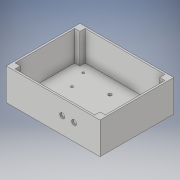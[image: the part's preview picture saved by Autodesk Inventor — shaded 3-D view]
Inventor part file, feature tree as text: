
AUTODESK INVENTOR PART (.ipt)
format: ipt  version: 2018 (Build 220112000, 112)  size: 164,352 bytes
history: native  units: in
note: dims shown in document units (in); Inventor stores cm internally (conversion verified against a paired STEP export)
features: extrude x5, sketch x5
ambient origin geometry x8: Origin, YZ Plane, XZ Plane, XY Plane, X Axis, Y Axis, Z Axis, Center Point
bodies: Solid1 (feature_tree)
feature tree (10):
  extrude  "Extrusion1"  Depth=3.701in
  extrude  "Extrusion2"  Depth=4.527in
  extrude  "Extrusion3"  Depth=0.354in
  extrude  "Extrusion6"  Depth=0.354in
  extrude  "Extrusion7"  Depth=1.5in TaperAngle=0.0deg
  sketch  "Sketch1"  dims[d0=4.705in d1=3.701in]
  sketch  "Sketch2"  dims[d2=0.089in d3=0.0in d4=4.527in]
  sketch  "Sketch3"  dims[d5=3.523in d6=0.354in]
  sketch  "Sketch7"  dims[d7=0.354in d10=0.354in]
  sketch  "Sketch8"  dims[d11=0.354in d14=1.5in d15=0.0in d18=0.164in d19=0.164in d20=0.0in d21=0.0in d48=0.787in d49=0.118in d50=0.118in d51=0.118in d52=0.118in d65=0.112in d66=0.112in d68=0.112in d69=0.0in d70=0.0in d74=0.25in d75=0.25in d76=0.0in d77=0.0in]
